# Revit family: 873-00-001-DN1600
name_source: partatom
category: Pipe Accessories
units: mm (PartAtom-declared; Revit-internal decimal feet)

## family parameters
Always vertical = Yes
Cut with Voids When Loaded = No
Part Type = Valve - Breaks Into
Round Connector Dimension = Use Diameter
Shared = No
Work Plane-Based = No

## types (2) — shared parameters
873-1600-00-041000 = DN1600_PN10
873-1600-00-141000 = DN1600_PN16
A = 385 mm  [stored 1.26312 ft]
Angle = 22.50°
Body_Wallthicknss = 10 mm  [stored 0.0328084 ft]
DN = 1600 mm  [stored 5.24934 ft]
Description_ = AVK DISMANTLING JOINT
Flange_thickness = 20 mm  [stored 0.0656168 ft]
Id(Radius) = 800 mm  [stored 2.62467 ft]
Search_table = 873-00-001-DN1600
URL product pages = https://www.avkvalves.com
d1 = 1820 mm  [stored 5.97113 ft]

## per-type parameters (varying)
| type | L | T | d2 |
| DN1600_PN10 | 600 mm  [stored 1.9685 ft] | 45 mm  [stored 0.147638 ft] | 958 mm |
| DN1600_PN16 | 700 mm  [stored 2.29659 ft] | 52 mm | 965 mm  [stored 3.16601 ft] |

note: [stored X ft] marks values corroborated as IEEE doubles in the binary element streams (Revit-internal decimal feet)

## geometry (parser evidence)
native form markers: Sweep x5
no freeform markers — native parametric forms only
